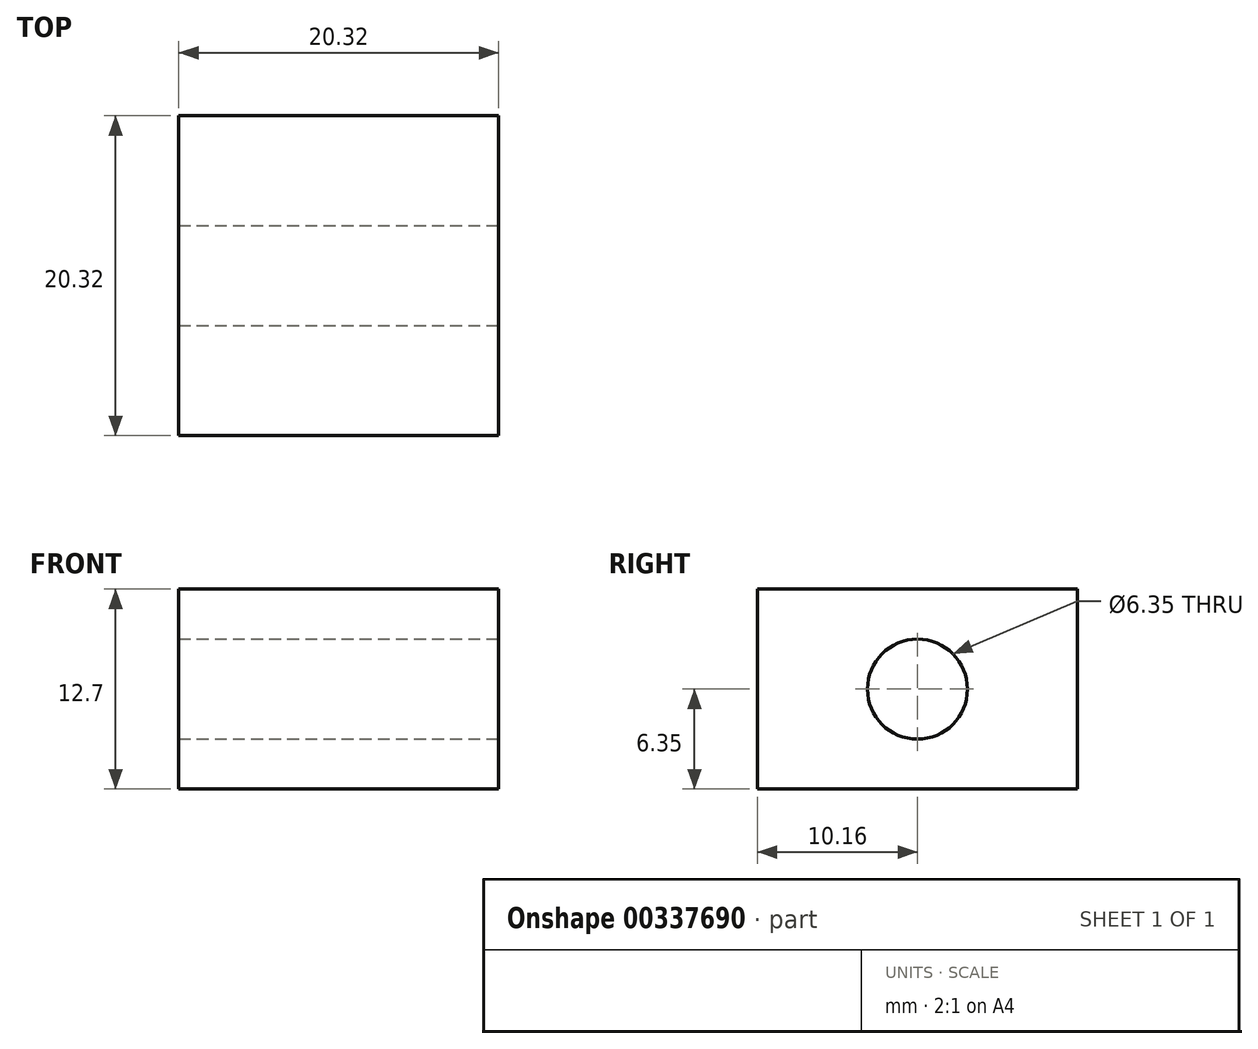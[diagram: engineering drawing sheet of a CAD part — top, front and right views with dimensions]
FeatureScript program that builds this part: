
annotation { "Feature Type Name" : "Feature", "Feature Type Description" : "" }
export const myFeature = defineFeature(function(context is Context, id is Id, definition is map)
    precondition{}
    {
        {
            var Q0;
            Q0=qCreatedBy(makeId("Front.planeOp"),FACE);
            var sketch = newSketch(context, id + "F0", { "sketchPlane" : qUnion([Q0])});
            skLineSegment(sketch, "E0.bottom", {"start": v(0, 0) * mm, "end": v(20.32, 0) * mm});
            skLineSegment(sketch, "E0.top", {"start": v(0, 12.7) * mm, "end": v(20.32, 12.7) * mm});
            skLineSegment(sketch, "E0.left", {"start": v(0, 0) * mm, "end": v(0, 12.7) * mm});
            skLineSegment(sketch, "E0.right", {"start": v(20.32, 0) * mm, "end": v(20.32, 12.7) * mm});
            skSolve(sketch);
        }
        {
            var Q0;
            Q0=makeQuery(id+"F0.imprint","IMPRINT",FACE,{"disambiguationData":[TD([[makeQuery(id+"F0.imprint","IMPRINT",EDGE,{"derivedFrom":sQuery(id+"F0.wireOp",EDGE,"E0.bottom")}),1.0]])]});
            extrude(context, id + "F1", {"entities" : qUnion([Q0]), "depth" : 20.32 * mm});
        }
        {
            var Q0;
            Q0=makeQuery(id+"F1.opExtrude","SWEPT_FACE",FACE,{"disambiguationData":[OSD([sQuery(id+"F0.wireOp",EDGE,"E0.right")])]});
            var sketch = newSketch(context, id + "F2", { "sketchPlane" : qUnion([Q0])});
            skLineSegment(sketch, "E1.bottom", {"start": v(0, 0) * mm, "end": v(-10.16, 0) * mm, "construction": true});
            skLineSegment(sketch, "E1.top", {"start": v(0, 6.35) * mm, "end": v(-10.16, 6.35) * mm, "construction": true});
            skLineSegment(sketch, "E1.left", {"start": v(0, 0) * mm, "end": v(0, 6.35) * mm, "construction": true});
            skLineSegment(sketch, "E1.right", {"start": v(-10.16, 0) * mm, "end": v(-10.16, 6.35) * mm, "construction": true});
            skCircle(sketch, "E2", {"center": v(-10.16, 6.35) * mm, "radius": 3.18 * mm});
            skSolve(sketch);
        }
        {
            var Q0;
            Q0=makeQuery(id+"F2.imprint","IMPRINT",FACE,{"disambiguationData":[TD([[makeQuery(id+"F2.imprint","IMPRINT",EDGE,{"derivedFrom":sQuery(id+"F2.wireOp",EDGE,"E2")}),1.0]])]});
            extrude(context, id + "F3", {"entities" : qUnion([Q0]), "operationType" : NewBodyOperationType.REMOVE, "oppositeDirection" : true, "depth" : 25.4 * mm});
        }
    });
